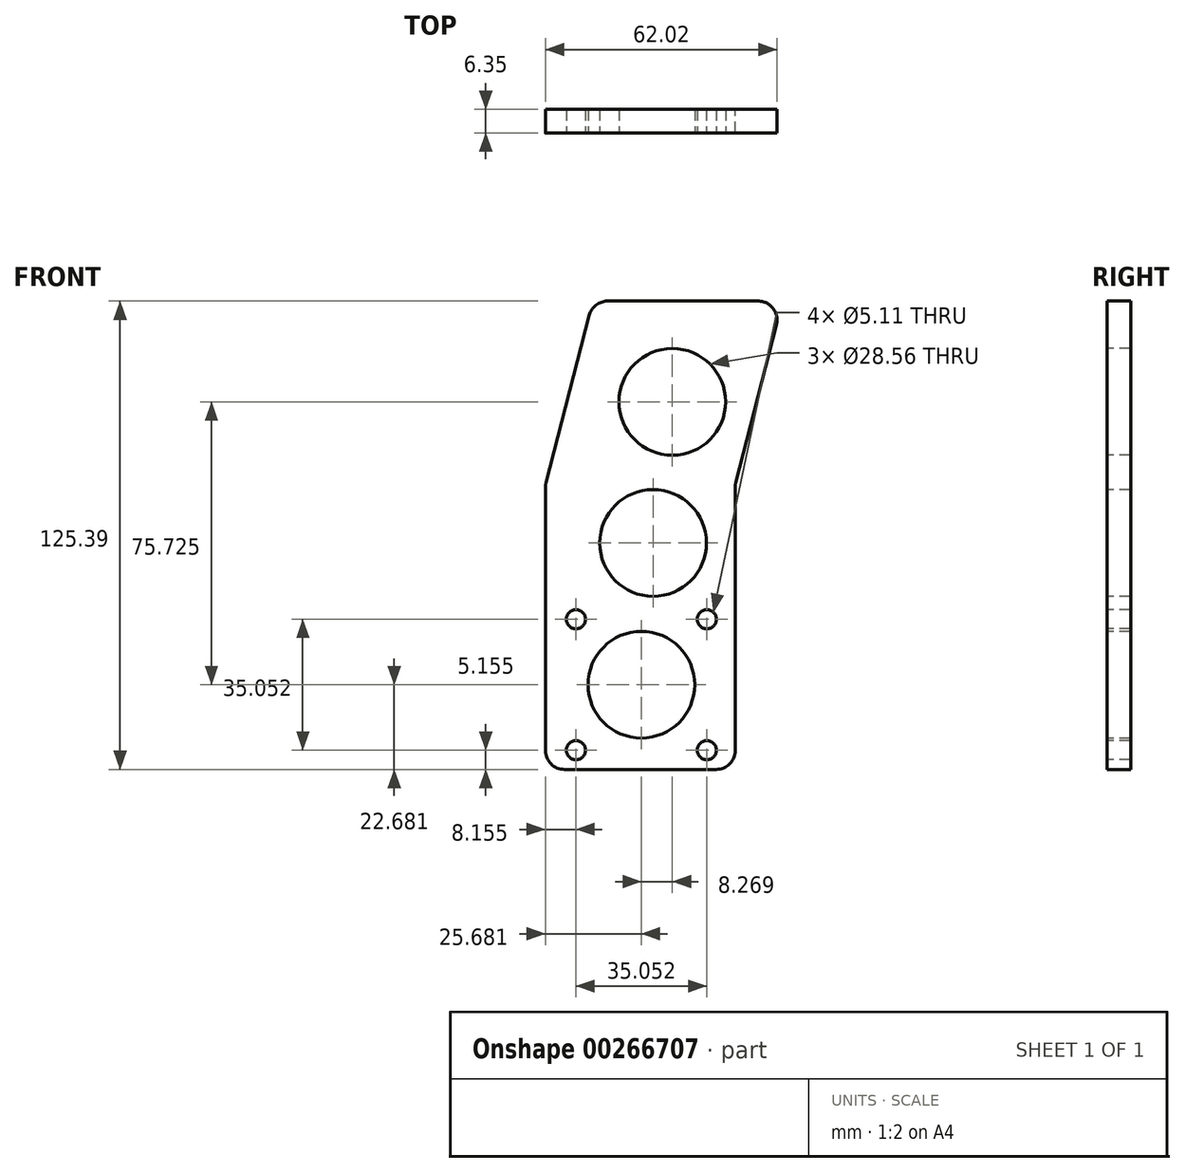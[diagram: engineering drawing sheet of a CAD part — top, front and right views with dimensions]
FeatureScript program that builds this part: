
annotation { "Feature Type Name" : "Feature", "Feature Type Description" : "" }
export const myFeature = defineFeature(function(context is Context, id is Id, definition is map)
    precondition{}
    {
        {
            var Q0;
            Q0=qCreatedBy(makeId("Front.planeOp"),FACE);
            var sketch = newSketch(context, id + "F0", { "sketchPlane" : qUnion([Q0])});
            skLineSegment(sketch, "E0.bottom", {"start": v(-80.1, 0) * mm, "end": v(-29.3, 0) * mm});
            skLineSegment(sketch, "E0.top", {"start": v(-80.1, -76.2) * mm, "end": v(-29.3, -76.2) * mm});
            skLineSegment(sketch, "E0.left", {"start": v(-80.1, 0) * mm, "end": v(-80.1, -76.2) * mm});
            skLineSegment(sketch, "E0.right", {"start": v(-29.3, 0) * mm, "end": v(-29.3, -76.2) * mm});
            skLineSegment(sketch, "E1", {"start": v(-29.3, 0) * mm, "end": v(-16.6, 49.19) * mm});
            skLineSegment(sketch, "E2", {"start": v(-16.6, 49.19) * mm, "end": v(-67.4, 49.19) * mm});
            skLineSegment(sketch, "E3", {"start": v(-67.4, 49.19) * mm, "end": v(-80.1, 0) * mm});
            skSolve(sketch);
        }
        {
            var Q0;
            Q0 = qSketchRegion(id + "F0", true);
            extrude(context, id + "F1", {"entities" : qUnion([Q0]), "depth" : 6.35 * mm});
        }
        {
            var Q0;
            Q0=makeQuery(id+"F1.opExtrude","CAP_FACE",FACE,{"disambiguationData":[OSD([sQuery(id+"F0.wireOp",EDGE,"E0.top"),sQuery(id+"F0.wireOp",EDGE,"E0.left"),sQuery(id+"F0.wireOp",EDGE,"E0.right"),sQuery(id+"F0.wireOp",EDGE,"E1"),sQuery(id+"F0.wireOp",EDGE,"E2"),sQuery(id+"F0.wireOp",EDGE,"E3")])],"isStart":false});
            var sketch = newSketch(context, id + "F2", { "sketchPlane" : qUnion([Q0])});
            skCircle(sketch, "E4", {"center": v(-46.16, 22.2) * mm, "radius": 14.28 * mm});
            skCircle(sketch, "E5", {"center": v(-51.27, -15.55) * mm, "radius": 14.9 * mm});
            skCircle(sketch, "E6", {"center": v(-54.43, -53.52) * mm, "radius": 14.28 * mm});
            skSolve(sketch);
        }
        {
            var Q0;
            Q0=sQuery(id+"F2.wireOp",VERTEX,"E4.center");
            var Q1;
            Q1=sQuery(id+"F2.wireOp",VERTEX,"E5.center");
            var Q2;
            Q2=sQuery(id+"F2.wireOp",VERTEX,"E6.center");
            var Q3;
            Q3=makeQuery(id+"F1.opExtrude","SWEPT_BODY",BODY,{"disambiguationData":[OSD([sQuery(id+"F0.wireOp",EDGE,"E0.top"),sQuery(id+"F0.wireOp",EDGE,"E0.left"),sQuery(id+"F0.wireOp",EDGE,"E0.right"),sQuery(id+"F0.wireOp",EDGE,"E1"),sQuery(id+"F0.wireOp",EDGE,"E2"),sQuery(id+"F0.wireOp",EDGE,"E3")])]});
            hole(context, id + "F3", {"style" : HoleStyle.SIMPLE, "endStyle" : HoleEndStyle.THROUGH, "holeDiameter" : 28.56 * mm, "tappedDepth" : 12.7 * mm, "tapClearance" : 3, "locations" : qUnion([Q0, Q1, Q2]), "scope" : qUnion([Q3])});
        }
        {
            var Q0;
            Q0=makeQuery(id+"F1.opExtrude","CAP_FACE",FACE,{"disambiguationData":[OSD([sQuery(id+"F0.wireOp",EDGE,"E0.top"),sQuery(id+"F0.wireOp",EDGE,"E0.left"),sQuery(id+"F0.wireOp",EDGE,"E0.right"),sQuery(id+"F0.wireOp",EDGE,"E1"),sQuery(id+"F0.wireOp",EDGE,"E2"),sQuery(id+"F0.wireOp",EDGE,"E3")])],"isStart":false});
            var sketch = newSketch(context, id + "F4", { "sketchPlane" : qUnion([Q0])});
            skLineSegment(sketch, "E7.bottom", {"start": v(-36.9, -36) * mm, "end": v(-71.96, -36) * mm, "construction": true});
            skLineSegment(sketch, "E7.top", {"start": v(-36.9, -71.04) * mm, "end": v(-71.96, -71.04) * mm, "construction": true});
            skLineSegment(sketch, "E7.left", {"start": v(-36.9, -36) * mm, "end": v(-36.9, -71.04) * mm, "construction": true});
            skLineSegment(sketch, "E7.right", {"start": v(-71.96, -36) * mm, "end": v(-71.96, -71.04) * mm, "construction": true});
            skPoint(sketch, "E7.middle", {"position": v(-54.43, -53.52) * mm});
            skCircle(sketch, "E8", {"center": v(-36.9, -36) * mm, "radius": 2.55 * mm});
            skCircle(sketch, "E9", {"center": v(-36.9, -71.04) * mm, "radius": 2.55 * mm});
            skCircle(sketch, "E10", {"center": v(-71.96, -71.04) * mm, "radius": 2.55 * mm});
            skCircle(sketch, "E11", {"center": v(-71.96, -36) * mm, "radius": 2.55 * mm});
            skSolve(sketch);
        }
        {
            var Q0;
            Q0=sQuery(id+"F4.wireOp",VERTEX,"E7.bottom.start");
            var Q1;
            Q1=sQuery(id+"F4.wireOp",VERTEX,"E7.top.start");
            var Q2;
            Q2=sQuery(id+"F4.wireOp",VERTEX,"E7.top.end");
            var Q3;
            Q3=sQuery(id+"F4.wireOp",VERTEX,"E7.bottom.end");
            var Q4;
            Q4=makeQuery(id+"F1.opExtrude","SWEPT_BODY",BODY,{"disambiguationData":[OSD([sQuery(id+"F0.wireOp",EDGE,"E0.top"),sQuery(id+"F0.wireOp",EDGE,"E0.left"),sQuery(id+"F0.wireOp",EDGE,"E0.right"),sQuery(id+"F0.wireOp",EDGE,"E1"),sQuery(id+"F0.wireOp",EDGE,"E2"),sQuery(id+"F0.wireOp",EDGE,"E3")])]});
            hole(context, id + "F5", {"style" : HoleStyle.SIMPLE, "endStyle" : HoleEndStyle.THROUGH, "holeDiameter" : 5.1 * mm, "tappedDepth" : 12.7 * mm, "tapClearance" : 3, "locations" : qUnion([Q0, Q1, Q2, Q3]), "scope" : qUnion([Q4])});
        }
        {
            var Q0;
            Q0=makeQuery(id+"F1.opExtrude","SWEPT_EDGE",EDGE,{"disambiguationData":[OSD([sQuery(id+"F0.wireOp",EDGE,"E2"),sQuery(id+"F0.wireOp",EDGE,"E3")])]});
            var Q1;
            Q1=makeQuery(id+"F1.opExtrude","SWEPT_EDGE",EDGE,{"disambiguationData":[OSD([sQuery(id+"F0.wireOp",EDGE,"E1"),sQuery(id+"F0.wireOp",EDGE,"E2")])]});
            var Q2;
            Q2=makeQuery(id+"F1.opExtrude","SWEPT_EDGE",EDGE,{"disambiguationData":[OSD([sQuery(id+"F0.wireOp",EDGE,"E0.bottom"),sQuery(id+"F0.wireOp",EDGE,"E0.left"),sQuery(id+"F0.wireOp",EDGE,"E3")])]});
            var Q3;
            Q3=makeQuery(id+"F1.opExtrude","SWEPT_EDGE",EDGE,{"disambiguationData":[OSD([sQuery(id+"F0.wireOp",EDGE,"E0.top"),sQuery(id+"F0.wireOp",EDGE,"E0.left")])]});
            var Q4;
            Q4=makeQuery(id+"F1.opExtrude","SWEPT_EDGE",EDGE,{"disambiguationData":[OSD([sQuery(id+"F0.wireOp",EDGE,"E0.top"),sQuery(id+"F0.wireOp",EDGE,"E0.right")])]});
            var Q5;
            Q5=makeQuery(id+"F1.opExtrude","SWEPT_EDGE",EDGE,{"disambiguationData":[OSD([sQuery(id+"F0.wireOp",EDGE,"E0.bottom"),sQuery(id+"F0.wireOp",EDGE,"E0.right"),sQuery(id+"F0.wireOp",EDGE,"E1")])]});
            fillet(context, id + "F6", {"entities" : qUnion([Q0, Q1, Q2, Q3, Q4, Q5]), "radius" : 5.08 * mm, "tangentPropagation" : true, "allowEdgeOverflow" : false});
        }
    });
